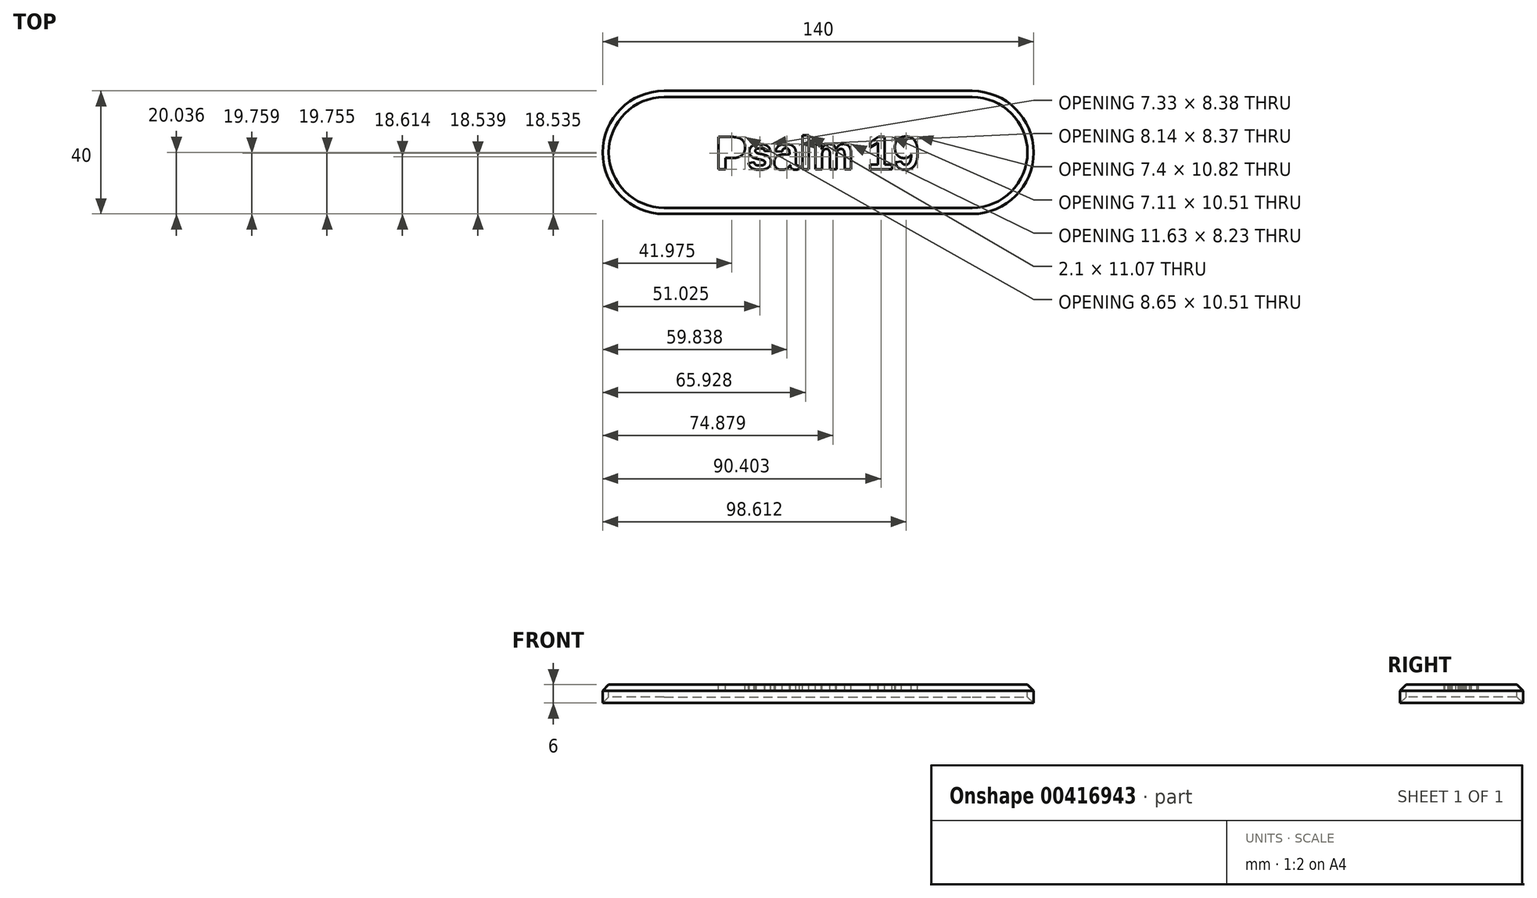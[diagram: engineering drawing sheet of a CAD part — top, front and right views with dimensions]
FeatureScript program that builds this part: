
annotation { "Feature Type Name" : "Feature", "Feature Type Description" : "" }
export const myFeature = defineFeature(function(context is Context, id is Id, definition is map)
    precondition{}
    {
        {
            assignVariable(context, id + "F0", {"name" : "THICKNESS", "anyValue" : 2});
        }
        {
            var Q0;
            Q0=qCreatedBy(makeId("Top.planeOp"),FACE);
            cPlane(context, id + "F1", {"entities" : qUnion([Q0]), "cplaneType" : CPlaneType.OFFSET, "offset" : 2 * mm, "oppositeDirection" : true, "width" : 150 * mm, "height" : 150 * mm});
        }
        {
            var Q0;
            Q0=qCreatedBy(makeId("Top.planeOp"),FACE);
            var sketch = newSketch(context, id + "F2", { "sketchPlane" : qUnion([Q0])});
            skLineSegment(sketch, "E0", {"start": v(50, 0) * mm, "end": v(-50, 0) * mm, "construction": true});
            skArc(sketch, "E1.0.startCap", {"start": v(50, 20) * mm, "mid": v(70, 0) * mm, "end": v(50, -20) * mm});
            skArc(sketch, "E1.0.endCap", {"start": v(-50, -20) * mm, "mid": v(-70, 0) * mm, "end": v(-50, 20) * mm});
            skLineSegment(sketch, "E1.0.left", {"start": v(50, -20) * mm, "end": v(-50, -20) * mm});
            skLineSegment(sketch, "E1.0.right", {"start": v(50, 20) * mm, "end": v(-50, 20) * mm});
            skText(sketch, "E2", { "text": "Psalm 19", "fontName": "Arimo-Bold.ttf"});
            const initialGuessF2  = {"E2": [-0.03337, -0.0055, 1, 0, 0.011]};
            skSetInitialGuess(sketch, initialGuessF2);
            skSolve(sketch);
        }
        {
            var Q0;
            Q0 = qSketchRegion(id + "F2", true);
            extrude(context, id + "F3", {"entities" : qUnion([Q0]), "oppositeDirection" : true, "depth" : (getVariable(context, 'THICKNESS') * 3) * mm});
        }
        {
            var Q0;
            Q0=qCreatedBy(id+"F1.planeOp",FACE);
            var sketch = newSketch(context, id + "F4", { "sketchPlane" : qUnion([Q0])});
            skLineSegment(sketch, "E3.0", {"start": v(-50, 18) * mm, "end": v(50, 18) * mm});
            skArc(sketch, "E3.1", {"start": v(50, 18) * mm, "mid": v(68, 0) * mm, "end": v(50, -18) * mm});
            skLineSegment(sketch, "E3.2", {"start": v(-50, -18) * mm, "end": v(50, -18) * mm});
            skArc(sketch, "E3.3", {"start": v(-50, -18) * mm, "mid": v(-68, 0) * mm, "end": v(-50, 18) * mm});
            skSolve(sketch);
        }
        {
            var Q0;
            Q0 = qSketchRegion(id + "F4", true);
            extrude(context, id + "F5", {"entities" : qUnion([Q0]), "operationType" : NewBodyOperationType.REMOVE, "endBound" : BoundingType.THROUGH_ALL, "oppositeDirection" : true, "depth" : 25 * mm});
        }
        {
            var Q0;
            Q0=makeQuery(id+"F3.opExtrude","CAP_EDGE",EDGE,{"disambiguationData":[OSD([sQuery(id+"F2.wireOp",EDGE,"E1.0.left")])],"isStart":true});
            var Q1;
            Q1=makeQuery(id+"F5.boolean.opBoolean","INTERSECT",EDGE,{"derivedFrom":[makeQuery(id+"F3.opExtrude","CAP_FACE",FACE,{"disambiguationData":[OSD([sQuery(id+"F2.wireOp",EDGE,"E1.0.startCap"),sQuery(id+"F2.wireOp",EDGE,"E1.0.endCap"),sQuery(id+"F2.wireOp",EDGE,"E1.0.left"),sQuery(id+"F2.wireOp",EDGE,"E1.0.right"),sQuery(id+"F2.wireOp",EDGE,"E2.sketch_text.stroke-0"),sQuery(id+"F2.wireOp",EDGE,"E2.sketch_text.stroke-1"),sQuery(id+"F2.wireOp",EDGE,"E2.sketch_text.stroke-2"),sQuery(id+"F2.wireOp",EDGE,"E2.sketch_text.stroke-3"),sQuery(id+"F2.wireOp",EDGE,"E2.sketch_text.stroke-4"),sQuery(id+"F2.wireOp",EDGE,"E2.sketch_text.stroke-5"),sQuery(id+"F2.wireOp",EDGE,"E2.sketch_text.stroke-6"),sQuery(id+"F2.wireOp",EDGE,"E2.sketch_text.stroke-7"),sQuery(id+"F2.wireOp",EDGE,"E2.sketch_text.stroke-8"),sQuery(id+"F2.wireOp",EDGE,"E2.sketch_text.stroke-9"),sQuery(id+"F2.wireOp",EDGE,"E2.sketch_text.stroke-10"),sQuery(id+"F2.wireOp",EDGE,"E2.sketch_text.stroke-11"),sQuery(id+"F2.wireOp",EDGE,"E2.sketch_text.stroke-12"),sQuery(id+"F2.wireOp",EDGE,"E2.sketch_text.stroke-13"),sQuery(id+"F2.wireOp",EDGE,"E2.sketch_text.stroke-14"),sQuery(id+"F2.wireOp",EDGE,"E2.sketch_text.stroke-15"),sQuery(id+"F2.wireOp",EDGE,"E2.sketch_text.stroke-16"),sQuery(id+"F2.wireOp",EDGE,"E2.sketch_text.stroke-17"),sQuery(id+"F2.wireOp",EDGE,"E2.sketch_text.stroke-18"),sQuery(id+"F2.wireOp",EDGE,"E2.sketch_text.stroke-19"),sQuery(id+"F2.wireOp",EDGE,"E2.sketch_text.stroke-20"),sQuery(id+"F2.wireOp",EDGE,"E2.sketch_text.stroke-21"),sQuery(id+"F2.wireOp",EDGE,"E2.sketch_text.stroke-22"),sQuery(id+"F2.wireOp",EDGE,"E2.sketch_text.stroke-23"),sQuery(id+"F2.wireOp",EDGE,"E2.sketch_text.stroke-24"),sQuery(id+"F2.wireOp",EDGE,"E2.sketch_text.stroke-25"),sQuery(id+"F2.wireOp",EDGE,"E2.sketch_text.stroke-26"),sQuery(id+"F2.wireOp",EDGE,"E2.sketch_text.stroke-27"),sQuery(id+"F2.wireOp",EDGE,"E2.sketch_text.stroke-28"),sQuery(id+"F2.wireOp",EDGE,"E2.sketch_text.stroke-29"),sQuery(id+"F2.wireOp",EDGE,"E2.sketch_text.stroke-30"),sQuery(id+"F2.wireOp",EDGE,"E2.sketch_text.stroke-31"),sQuery(id+"F2.wireOp",EDGE,"E2.sketch_text.stroke-32"),sQuery(id+"F2.wireOp",EDGE,"E2.sketch_text.stroke-33"),sQuery(id+"F2.wireOp",EDGE,"E2.sketch_text.stroke-34"),sQuery(id+"F2.wireOp",EDGE,"E2.sketch_text.stroke-35"),sQuery(id+"F2.wireOp",EDGE,"E2.sketch_text.stroke-36"),sQuery(id+"F2.wireOp",EDGE,"E2.sketch_text.stroke-37"),sQuery(id+"F2.wireOp",EDGE,"E2.sketch_text.stroke-38"),sQuery(id+"F2.wireOp",EDGE,"E2.sketch_text.stroke-39"),sQuery(id+"F2.wireOp",EDGE,"E2.sketch_text.stroke-40"),sQuery(id+"F2.wireOp",EDGE,"E2.sketch_text.stroke-41"),sQuery(id+"F2.wireOp",EDGE,"E2.sketch_text.stroke-42"),sQuery(id+"F2.wireOp",EDGE,"E2.sketch_text.stroke-43"),sQuery(id+"F2.wireOp",EDGE,"E2.sketch_text.stroke-44"),sQuery(id+"F2.wireOp",EDGE,"E2.sketch_text.stroke-45"),sQuery(id+"F2.wireOp",EDGE,"E2.sketch_text.stroke-46"),sQuery(id+"F2.wireOp",EDGE,"E2.sketch_text.stroke-47"),sQuery(id+"F2.wireOp",EDGE,"E2.sketch_text.stroke-48"),sQuery(id+"F2.wireOp",EDGE,"E2.sketch_text.stroke-49"),sQuery(id+"F2.wireOp",EDGE,"E2.sketch_text.stroke-50"),sQuery(id+"F2.wireOp",EDGE,"E2.sketch_text.stroke-51"),sQuery(id+"F2.wireOp",EDGE,"E2.sketch_text.stroke-52"),sQuery(id+"F2.wireOp",EDGE,"E2.sketch_text.stroke-53"),sQuery(id+"F2.wireOp",EDGE,"E2.sketch_text.stroke-54"),sQuery(id+"F2.wireOp",EDGE,"E2.sketch_text.stroke-55"),sQuery(id+"F2.wireOp",EDGE,"E2.sketch_text.stroke-56"),sQuery(id+"F2.wireOp",EDGE,"E2.sketch_text.stroke-57"),sQuery(id+"F2.wireOp",EDGE,"E2.sketch_text.stroke-58"),sQuery(id+"F2.wireOp",EDGE,"E2.sketch_text.stroke-59"),sQuery(id+"F2.wireOp",EDGE,"E2.sketch_text.stroke-65"),sQuery(id+"F2.wireOp",EDGE,"E2.sketch_text.stroke-66"),sQuery(id+"F2.wireOp",EDGE,"E2.sketch_text.stroke-67"),sQuery(id+"F2.wireOp",EDGE,"E2.sketch_text.stroke-68"),sQuery(id+"F2.wireOp",EDGE,"E2.sketch_text.stroke-69"),sQuery(id+"F2.wireOp",EDGE,"E2.sketch_text.stroke-70"),sQuery(id+"F2.wireOp",EDGE,"E2.sketch_text.stroke-71"),sQuery(id+"F2.wireOp",EDGE,"E2.sketch_text.stroke-72"),sQuery(id+"F2.wireOp",EDGE,"E2.sketch_text.stroke-73"),sQuery(id+"F2.wireOp",EDGE,"E2.sketch_text.stroke-74"),sQuery(id+"F2.wireOp",EDGE,"E2.sketch_text.stroke-75"),sQuery(id+"F2.wireOp",EDGE,"E2.sketch_text.stroke-76"),sQuery(id+"F2.wireOp",EDGE,"E2.sketch_text.stroke-77"),sQuery(id+"F2.wireOp",EDGE,"E2.sketch_text.stroke-78"),sQuery(id+"F2.wireOp",EDGE,"E2.sketch_text.stroke-79"),sQuery(id+"F2.wireOp",EDGE,"E2.sketch_text.stroke-80"),sQuery(id+"F2.wireOp",EDGE,"E2.sketch_text.stroke-81"),sQuery(id+"F2.wireOp",EDGE,"E2.sketch_text.stroke-82"),sQuery(id+"F2.wireOp",EDGE,"E2.sketch_text.stroke-83"),sQuery(id+"F2.wireOp",EDGE,"E2.sketch_text.stroke-84"),sQuery(id+"F2.wireOp",EDGE,"E2.sketch_text.stroke-85"),sQuery(id+"F2.wireOp",EDGE,"E2.sketch_text.stroke-86"),sQuery(id+"F2.wireOp",EDGE,"E2.sketch_text.stroke-87"),sQuery(id+"F2.wireOp",EDGE,"E2.sketch_text.stroke-88"),sQuery(id+"F2.wireOp",EDGE,"E2.sketch_text.stroke-89"),sQuery(id+"F2.wireOp",EDGE,"E2.sketch_text.stroke-90"),sQuery(id+"F2.wireOp",EDGE,"E2.sketch_text.stroke-91"),sQuery(id+"F2.wireOp",EDGE,"E2.sketch_text.stroke-92"),sQuery(id+"F2.wireOp",EDGE,"E2.sketch_text.stroke-93"),sQuery(id+"F2.wireOp",EDGE,"E2.sketch_text.stroke-94"),sQuery(id+"F2.wireOp",EDGE,"E2.sketch_text.stroke-95"),sQuery(id+"F2.wireOp",EDGE,"E2.sketch_text.stroke-96"),sQuery(id+"F2.wireOp",EDGE,"E2.sketch_text.stroke-97"),sQuery(id+"F2.wireOp",EDGE,"E2.sketch_text.stroke-98"),sQuery(id+"F2.wireOp",EDGE,"E2.sketch_text.stroke-99"),sQuery(id+"F2.wireOp",EDGE,"E2.sketch_text.stroke-100"),sQuery(id+"F2.wireOp",EDGE,"E2.sketch_text.stroke-101"),sQuery(id+"F2.wireOp",EDGE,"E2.sketch_text.stroke-102"),sQuery(id+"F2.wireOp",EDGE,"E2.sketch_text.stroke-103"),sQuery(id+"F2.wireOp",EDGE,"E2.sketch_text.stroke-104"),sQuery(id+"F2.wireOp",EDGE,"E2.sketch_text.stroke-105"),sQuery(id+"F2.wireOp",EDGE,"E2.sketch_text.stroke-106"),sQuery(id+"F2.wireOp",EDGE,"E2.sketch_text.stroke-107"),sQuery(id+"F2.wireOp",EDGE,"E2.sketch_text.stroke-108"),sQuery(id+"F2.wireOp",EDGE,"E2.sketch_text.stroke-109"),sQuery(id+"F2.wireOp",EDGE,"E2.sketch_text.stroke-110"),sQuery(id+"F2.wireOp",EDGE,"E2.sketch_text.stroke-111"),sQuery(id+"F2.wireOp",EDGE,"E2.sketch_text.stroke-112"),sQuery(id+"F2.wireOp",EDGE,"E2.sketch_text.stroke-113"),sQuery(id+"F2.wireOp",EDGE,"E2.sketch_text.stroke-114"),sQuery(id+"F2.wireOp",EDGE,"E2.sketch_text.stroke-115"),sQuery(id+"F2.wireOp",EDGE,"E2.sketch_text.stroke-116"),sQuery(id+"F2.wireOp",EDGE,"E2.sketch_text.stroke-117"),sQuery(id+"F2.wireOp",EDGE,"E2.sketch_text.stroke-118"),sQuery(id+"F2.wireOp",EDGE,"E2.sketch_text.stroke-119"),sQuery(id+"F2.wireOp",EDGE,"E2.sketch_text.stroke-120"),sQuery(id+"F2.wireOp",EDGE,"E2.sketch_text.stroke-121"),sQuery(id+"F2.wireOp",EDGE,"E2.sketch_text.stroke-122"),sQuery(id+"F2.wireOp",EDGE,"E2.sketch_text.stroke-123"),sQuery(id+"F2.wireOp",EDGE,"E2.sketch_text.stroke-124"),sQuery(id+"F2.wireOp",EDGE,"E2.sketch_text.stroke-125"),sQuery(id+"F2.wireOp",EDGE,"E2.sketch_text.stroke-126"),sQuery(id+"F2.wireOp",EDGE,"E2.sketch_text.stroke-127"),sQuery(id+"F2.wireOp",EDGE,"E2.sketch_text.stroke-128"),sQuery(id+"F2.wireOp",EDGE,"E2.sketch_text.stroke-129"),sQuery(id+"F2.wireOp",EDGE,"E2.sketch_text.stroke-130"),sQuery(id+"F2.wireOp",EDGE,"E2.sketch_text.stroke-131"),sQuery(id+"F2.wireOp",EDGE,"E2.sketch_text.stroke-132"),sQuery(id+"F2.wireOp",EDGE,"E2.sketch_text.stroke-133"),sQuery(id+"F2.wireOp",EDGE,"E2.sketch_text.stroke-134"),sQuery(id+"F2.wireOp",EDGE,"E2.sketch_text.stroke-135"),sQuery(id+"F2.wireOp",EDGE,"E2.sketch_text.stroke-136"),sQuery(id+"F2.wireOp",EDGE,"E2.sketch_text.stroke-137"),sQuery(id+"F2.wireOp",EDGE,"E2.sketch_text.stroke-138"),sQuery(id+"F2.wireOp",EDGE,"E2.sketch_text.stroke-139"),sQuery(id+"F2.wireOp",EDGE,"E2.sketch_text.stroke-140"),sQuery(id+"F2.wireOp",EDGE,"E2.sketch_text.stroke-141"),sQuery(id+"F2.wireOp",EDGE,"E2.sketch_text.stroke-142"),sQuery(id+"F2.wireOp",EDGE,"E2.sketch_text.stroke-143"),sQuery(id+"F2.wireOp",EDGE,"E2.sketch_text.stroke-144"),sQuery(id+"F2.wireOp",EDGE,"E2.sketch_text.stroke-145"),sQuery(id+"F2.wireOp",EDGE,"E2.sketch_text.stroke-146"),sQuery(id+"F2.wireOp",EDGE,"E2.sketch_text.stroke-147"),sQuery(id+"F2.wireOp",EDGE,"E2.sketch_text.stroke-148"),sQuery(id+"F2.wireOp",EDGE,"E2.sketch_text.stroke-149"),sQuery(id+"F2.wireOp",EDGE,"E2.sketch_text.stroke-150"),sQuery(id+"F2.wireOp",EDGE,"E2.sketch_text.stroke-161"),sQuery(id+"F2.wireOp",EDGE,"E2.sketch_text.stroke-162"),sQuery(id+"F2.wireOp",EDGE,"E2.sketch_text.stroke-163"),sQuery(id+"F2.wireOp",EDGE,"E2.sketch_text.stroke-164"),sQuery(id+"F2.wireOp",EDGE,"E2.sketch_text.stroke-165"),sQuery(id+"F2.wireOp",EDGE,"E2.sketch_text.stroke-166"),sQuery(id+"F2.wireOp",EDGE,"E2.sketch_text.stroke-167"),sQuery(id+"F2.wireOp",EDGE,"E2.sketch_text.stroke-168"),sQuery(id+"F2.wireOp",EDGE,"E2.sketch_text.stroke-169"),sQuery(id+"F2.wireOp",EDGE,"E2.sketch_text.stroke-170"),sQuery(id+"F2.wireOp",EDGE,"E2.sketch_text.stroke-171"),sQuery(id+"F2.wireOp",EDGE,"E2.sketch_text.stroke-172"),sQuery(id+"F2.wireOp",EDGE,"E2.sketch_text.stroke-179"),sQuery(id+"F2.wireOp",EDGE,"E2.sketch_text.stroke-180"),sQuery(id+"F2.wireOp",EDGE,"E2.sketch_text.stroke-181"),sQuery(id+"F2.wireOp",EDGE,"E2.sketch_text.stroke-182"),sQuery(id+"F2.wireOp",EDGE,"E2.sketch_text.stroke-183"),sQuery(id+"F2.wireOp",EDGE,"E2.sketch_text.stroke-184"),sQuery(id+"F2.wireOp",EDGE,"E2.sketch_text.stroke-185"),sQuery(id+"F2.wireOp",EDGE,"E2.sketch_text.stroke-186"),sQuery(id+"F2.wireOp",EDGE,"E2.sketch_text.stroke-187"),sQuery(id+"F2.wireOp",EDGE,"E2.sketch_text.stroke-188"),sQuery(id+"F2.wireOp",EDGE,"E2.sketch_text.stroke-189"),sQuery(id+"F2.wireOp",EDGE,"E2.sketch_text.stroke-190"),sQuery(id+"F2.wireOp",EDGE,"E2.sketch_text.stroke-191"),sQuery(id+"F2.wireOp",EDGE,"E2.sketch_text.stroke-192"),sQuery(id+"F2.wireOp",EDGE,"E2.sketch_text.stroke-193"),sQuery(id+"F2.wireOp",EDGE,"E2.sketch_text.stroke-194"),sQuery(id+"F2.wireOp",EDGE,"E2.sketch_text.stroke-195"),sQuery(id+"F2.wireOp",EDGE,"E2.sketch_text.stroke-196"),sQuery(id+"F2.wireOp",EDGE,"E2.sketch_text.stroke-197"),sQuery(id+"F2.wireOp",EDGE,"E2.sketch_text.stroke-198"),sQuery(id+"F2.wireOp",EDGE,"E2.sketch_text.stroke-199"),sQuery(id+"F2.wireOp",EDGE,"E2.sketch_text.stroke-200"),sQuery(id+"F2.wireOp",EDGE,"E2.sketch_text.stroke-201"),sQuery(id+"F2.wireOp",EDGE,"E2.sketch_text.stroke-202"),sQuery(id+"F2.wireOp",EDGE,"E2.sketch_text.stroke-203"),sQuery(id+"F2.wireOp",EDGE,"E2.sketch_text.stroke-204"),sQuery(id+"F2.wireOp",EDGE,"E2.sketch_text.stroke-205"),sQuery(id+"F2.wireOp",EDGE,"E2.sketch_text.stroke-206"),sQuery(id+"F2.wireOp",EDGE,"E2.sketch_text.stroke-207"),sQuery(id+"F2.wireOp",EDGE,"E2.sketch_text.stroke-208"),sQuery(id+"F2.wireOp",EDGE,"E2.sketch_text.stroke-209"),sQuery(id+"F2.wireOp",EDGE,"E2.sketch_text.stroke-210"),sQuery(id+"F2.wireOp",EDGE,"E2.sketch_text.stroke-211"),sQuery(id+"F2.wireOp",EDGE,"E2.sketch_text.stroke-212"),sQuery(id+"F2.wireOp",EDGE,"E2.sketch_text.stroke-213"),sQuery(id+"F2.wireOp",EDGE,"E2.sketch_text.stroke-214"),sQuery(id+"F2.wireOp",EDGE,"E2.sketch_text.stroke-215"),sQuery(id+"F2.wireOp",EDGE,"E2.sketch_text.stroke-216"),sQuery(id+"F2.wireOp",EDGE,"E2.sketch_text.stroke-217"),sQuery(id+"F2.wireOp",EDGE,"E2.sketch_text.stroke-218"),sQuery(id+"F2.wireOp",EDGE,"E2.sketch_text.stroke-219"),sQuery(id+"F2.wireOp",EDGE,"E2.sketch_text.stroke-220"),sQuery(id+"F2.wireOp",EDGE,"E2.sketch_text.stroke-221"),sQuery(id+"F2.wireOp",EDGE,"E2.sketch_text.stroke-222"),sQuery(id+"F2.wireOp",EDGE,"E2.sketch_text.stroke-223"),sQuery(id+"F2.wireOp",EDGE,"E2.sketch_text.stroke-224"),sQuery(id+"F2.wireOp",EDGE,"E2.sketch_text.stroke-225"),sQuery(id+"F2.wireOp",EDGE,"E2.sketch_text.stroke-226"),sQuery(id+"F2.wireOp",EDGE,"E2.sketch_text.stroke-227"),sQuery(id+"F2.wireOp",EDGE,"E2.sketch_text.stroke-228"),sQuery(id+"F2.wireOp",EDGE,"E2.sketch_text.stroke-229"),sQuery(id+"F2.wireOp",EDGE,"E2.sketch_text.stroke-230"),sQuery(id+"F2.wireOp",EDGE,"E2.sketch_text.stroke-231"),sQuery(id+"F2.wireOp",EDGE,"E2.sketch_text.stroke-232"),sQuery(id+"F2.wireOp",EDGE,"E2.sketch_text.stroke-233"),sQuery(id+"F2.wireOp",EDGE,"E2.sketch_text.stroke-244"),sQuery(id+"F2.wireOp",EDGE,"E2.sketch_text.stroke-245"),sQuery(id+"F2.wireOp",EDGE,"E2.sketch_text.stroke-246"),sQuery(id+"F2.wireOp",EDGE,"E2.sketch_text.stroke-247"),sQuery(id+"F2.wireOp",EDGE,"E2.sketch_text.stroke-248"),sQuery(id+"F2.wireOp",EDGE,"E2.sketch_text.stroke-249"),sQuery(id+"F2.wireOp",EDGE,"E2.sketch_text.stroke-250"),sQuery(id+"F2.wireOp",EDGE,"E2.sketch_text.stroke-251"),sQuery(id+"F2.wireOp",EDGE,"E2.sketch_text.stroke-252"),sQuery(id+"F2.wireOp",EDGE,"E2.sketch_text.stroke-253"),sQuery(id+"F2.wireOp",EDGE,"E2.sketch_text.stroke-254"),sQuery(id+"F2.wireOp",EDGE,"E2.sketch_text.stroke-255"),sQuery(id+"F2.wireOp",EDGE,"E2.sketch_text.stroke-256"),sQuery(id+"F2.wireOp",EDGE,"E2.sketch_text.stroke-257"),sQuery(id+"F2.wireOp",EDGE,"E2.sketch_text.stroke-258"),sQuery(id+"F2.wireOp",EDGE,"E2.sketch_text.stroke-259"),sQuery(id+"F2.wireOp",EDGE,"E2.sketch_text.stroke-260"),sQuery(id+"F2.wireOp",EDGE,"E2.sketch_text.stroke-261"),sQuery(id+"F2.wireOp",EDGE,"E2.sketch_text.stroke-262"),sQuery(id+"F2.wireOp",EDGE,"E2.sketch_text.stroke-263"),sQuery(id+"F2.wireOp",EDGE,"E2.sketch_text.stroke-264"),sQuery(id+"F2.wireOp",EDGE,"E2.sketch_text.stroke-265"),sQuery(id+"F2.wireOp",EDGE,"E2.sketch_text.stroke-266"),sQuery(id+"F2.wireOp",EDGE,"E2.sketch_text.stroke-267"),sQuery(id+"F2.wireOp",EDGE,"E2.sketch_text.stroke-268"),sQuery(id+"F2.wireOp",EDGE,"E2.sketch_text.stroke-269"),sQuery(id+"F2.wireOp",EDGE,"E2.sketch_text.stroke-270"),sQuery(id+"F2.wireOp",EDGE,"E2.sketch_text.stroke-271"),sQuery(id+"F2.wireOp",EDGE,"E2.sketch_text.stroke-272"),sQuery(id+"F2.wireOp",EDGE,"E2.sketch_text.stroke-273"),sQuery(id+"F2.wireOp",EDGE,"E2.sketch_text.stroke-274"),sQuery(id+"F2.wireOp",EDGE,"E2.sketch_text.stroke-275"),sQuery(id+"F2.wireOp",EDGE,"E2.sketch_text.stroke-276"),sQuery(id+"F2.wireOp",EDGE,"E2.sketch_text.stroke-277"),sQuery(id+"F2.wireOp",EDGE,"E2.sketch_text.stroke-278"),sQuery(id+"F2.wireOp",EDGE,"E2.sketch_text.stroke-279"),sQuery(id+"F2.wireOp",EDGE,"E2.sketch_text.stroke-280"),sQuery(id+"F2.wireOp",EDGE,"E2.sketch_text.stroke-281"),sQuery(id+"F2.wireOp",EDGE,"E2.sketch_text.stroke-282"),sQuery(id+"F2.wireOp",EDGE,"E2.sketch_text.stroke-283"),sQuery(id+"F2.wireOp",EDGE,"E2.sketch_text.stroke-284"),sQuery(id+"F2.wireOp",EDGE,"E2.sketch_text.stroke-285"),sQuery(id+"F2.wireOp",EDGE,"E2.sketch_text.stroke-286"),sQuery(id+"F2.wireOp",EDGE,"E2.sketch_text.stroke-287"),sQuery(id+"F2.wireOp",EDGE,"E2.sketch_text.stroke-288"),sQuery(id+"F2.wireOp",EDGE,"E2.sketch_text.stroke-289"),sQuery(id+"F2.wireOp",EDGE,"E2.sketch_text.stroke-290"),sQuery(id+"F2.wireOp",EDGE,"E2.sketch_text.stroke-291"),sQuery(id+"F2.wireOp",EDGE,"E2.sketch_text.stroke-292"),sQuery(id+"F2.wireOp",EDGE,"E2.sketch_text.stroke-293"),sQuery(id+"F2.wireOp",EDGE,"E2.sketch_text.stroke-294"),sQuery(id+"F2.wireOp",EDGE,"E2.sketch_text.stroke-295"),sQuery(id+"F2.wireOp",EDGE,"E2.sketch_text.stroke-296"),sQuery(id+"F2.wireOp",EDGE,"E2.sketch_text.stroke-297"),sQuery(id+"F2.wireOp",EDGE,"E2.sketch_text.stroke-298"),sQuery(id+"F2.wireOp",EDGE,"E2.sketch_text.stroke-299"),sQuery(id+"F2.wireOp",EDGE,"E2.sketch_text.stroke-300"),sQuery(id+"F2.wireOp",EDGE,"E2.sketch_text.stroke-301"),sQuery(id+"F2.wireOp",EDGE,"E2.sketch_text.stroke-302")])],"isStart":false}),makeQuery(id+"F5.opExtrude","SWEPT_FACE",FACE,{"disambiguationData":[OSD([sQuery(id+"F4.wireOp",EDGE,"E3.0")])]})]});
            chamfer(context, id + "F6", {"entities" : qUnion([Q0, Q1]), "width" : (getVariable(context, 'THICKNESS')) * mm, "tangentPropagation" : true});
        }
    });
